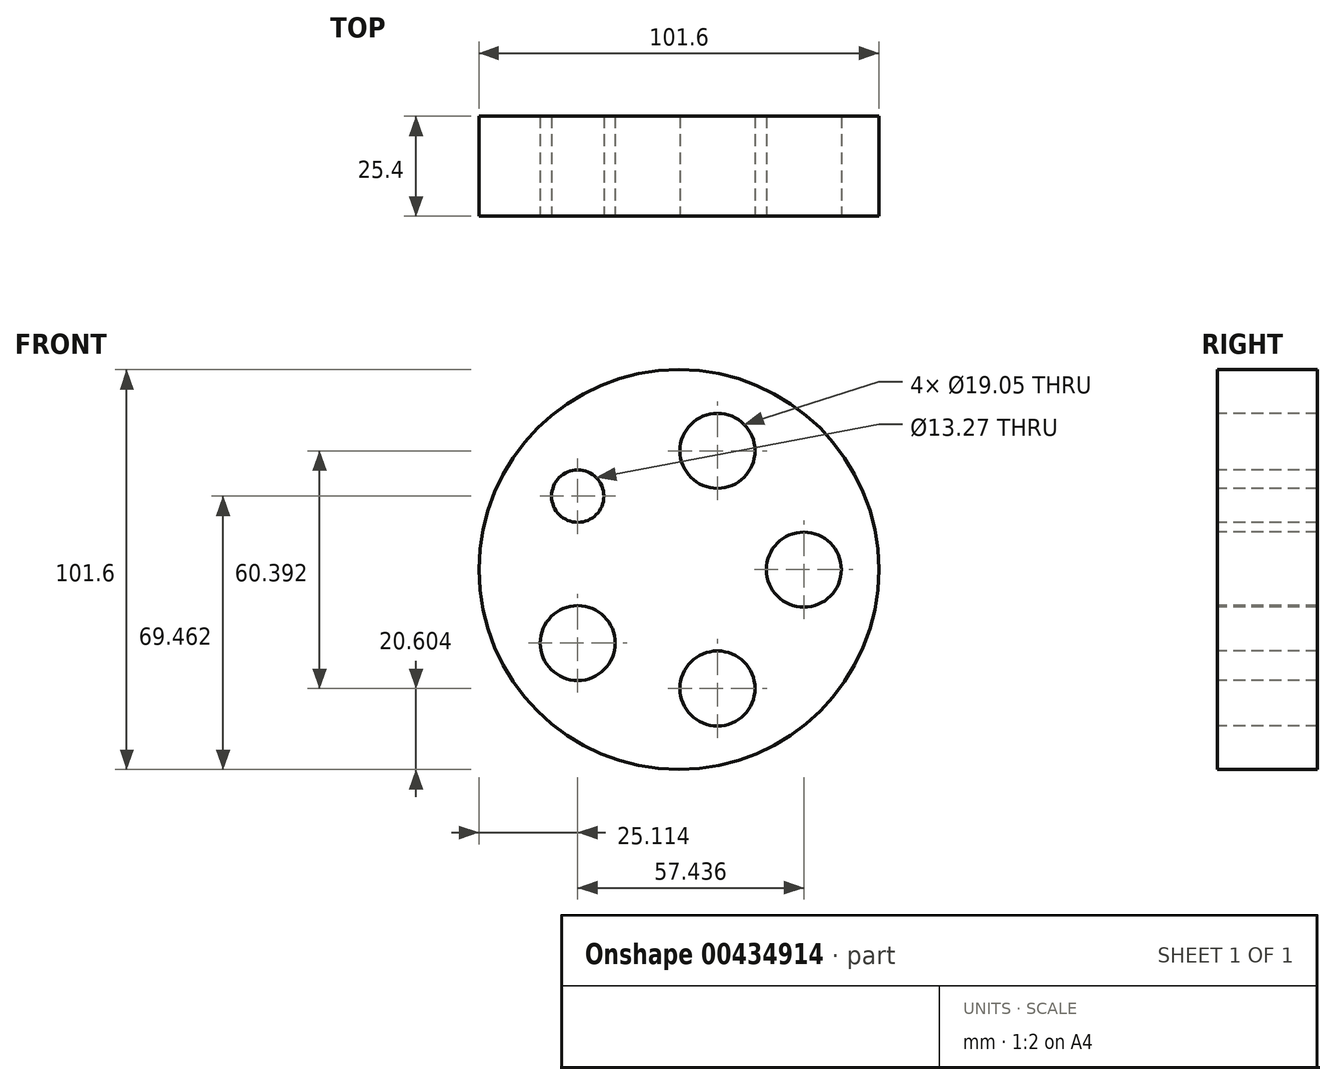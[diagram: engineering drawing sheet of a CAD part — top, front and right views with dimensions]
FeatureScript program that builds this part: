
annotation { "Feature Type Name" : "Feature", "Feature Type Description" : "" }
export const myFeature = defineFeature(function(context is Context, id is Id, definition is map)
    precondition{}
    {
        {
            var Q0;
            Q0=qCreatedBy(makeId("Front.planeOp"),FACE);
            var sketch = newSketch(context, id + "F0", { "sketchPlane" : qUnion([Q0])});
            skCircle(sketch, "E0", {"center": v(0, 0) * mm, "radius": 50.8 * mm});
            skCircle(sketch, "E1", {"center": v(0, 0) * mm, "radius": 31.75 * mm, "construction": true});
            skLineSegment(sketch, "E2.0", {"start": v(31.75, 0) * mm, "end": v(15.88, -27.5) * mm});
            skLineSegment(sketch, "E2.1", {"start": v(15.88, -27.5) * mm, "end": v(-15.87, -27.5) * mm});
            skLineSegment(sketch, "E2.2", {"start": v(-15.87, -27.5) * mm, "end": v(-31.75, 0) * mm});
            skLineSegment(sketch, "E2.3", {"start": v(-31.75, 0) * mm, "end": v(-15.88, 27.5) * mm});
            skLineSegment(sketch, "E2.4", {"start": v(-15.88, 27.5) * mm, "end": v(15.87, 27.5) * mm});
            skLineSegment(sketch, "E2.5", {"start": v(15.87, 27.5) * mm, "end": v(31.75, 0) * mm});
            skSolve(sketch);
        }
        {
            var Q0;
            Q0 = qSketchRegion(id + "F0", true);
            var Q1;
            Q1=makeQuery(id+"F0.imprint","IMPRINT",FACE,{"disambiguationData":[TD([[makeQuery(id+"F0.imprint","IMPRINT",EDGE,{"derivedFrom":sQuery(id+"F0.wireOp",EDGE,"E2.0")}),-1.0]])]});
            extrude(context, id + "F1", {"entities" : qUnion([Q0, Q1]), "depth" : 25.4 * mm});
        }
        {
            var Q0;
            Q0=makeQuery(id+"F1.opExtrude","CAP_FACE",FACE,{"disambiguationData":[OSD([sQuery(id+"F0.wireOp",EDGE,"E0")])],"isStart":false});
            var sketch = newSketch(context, id + "F2", { "sketchPlane" : qUnion([Q0])});
            skCircle(sketch, "E3", {"center": v(0, 0) * mm, "radius": 31.75 * mm, "construction": true});
            skLineSegment(sketch, "E4.0", {"start": v(31.75, 0) * mm, "end": v(9.81, -30.2) * mm});
            skLineSegment(sketch, "E4.1", {"start": v(9.81, -30.2) * mm, "end": v(-25.69, -18.66) * mm});
            skLineSegment(sketch, "E4.2", {"start": v(-25.69, -18.66) * mm, "end": v(-25.69, 18.66) * mm});
            skLineSegment(sketch, "E4.3", {"start": v(-25.69, 18.66) * mm, "end": v(9.81, 30.2) * mm});
            skLineSegment(sketch, "E4.4", {"start": v(9.81, 30.2) * mm, "end": v(31.75, 0) * mm});
            skCircle(sketch, "E5", {"center": v(9.81, 30.2) * mm, "radius": 3.18 * mm});
            skCircle(sketch, "E6", {"center": v(31.75, 0) * mm, "radius": 9.53 * mm});
            skCircle(sketch, "E7", {"center": v(9.81, -30.2) * mm, "radius": 9.53 * mm});
            skCircle(sketch, "E8", {"center": v(-25.69, 18.66) * mm, "radius": 9.53 * mm});
            skCircle(sketch, "E9", {"center": v(-25.69, -18.66) * mm, "radius": 8.93 * mm});
            skSolve(sketch);
        }
        {
            var Q0;
            Q0=sQuery(id+"F2.wireOp",VERTEX,"E5.center");
            var Q1;
            Q1=sQuery(id+"F2.wireOp",VERTEX,"E6.center");
            var Q2;
            Q2=sQuery(id+"F2.wireOp",VERTEX,"E9.center");
            var Q3;
            Q3=sQuery(id+"F2.wireOp",VERTEX,"E7.center");
            var Q4;
            Q4=makeQuery(id+"F1.opExtrude","SWEPT_BODY",BODY,{"disambiguationData":[OSD([sQuery(id+"F0.wireOp",EDGE,"E0")])]});
            hole(context, id + "F3", {"style" : HoleStyle.SIMPLE, "endStyle" : HoleEndStyle.THROUGH, "holeDiameter" : 19.05 * mm, "isTappedThrough" : true, "tappedDepth" : 12.7 * mm, "tapClearance" : 3, "locations" : qUnion([Q0, Q1, Q2, Q3]), "scope" : qUnion([Q4])});
        }
        {
            var Q0;
            Q0=makeQuery(id+"F1.opExtrude","CAP_FACE",FACE,{"disambiguationData":[OSD([sQuery(id+"F0.wireOp",EDGE,"E0")])],"isStart":false});
            var sketch = newSketch(context, id + "F4", { "sketchPlane" : qUnion([Q0])});
            skCircle(sketch, "E10.cCircle", {"center": v(0, 0) * mm, "radius": 31.75 * mm, "construction": true});
            skLineSegment(sketch, "E10.0", {"start": v(9.81, 30.2) * mm, "end": v(31.75, 0) * mm, "construction": true});
            skLineSegment(sketch, "E10.1", {"start": v(31.75, 0) * mm, "end": v(9.81, -30.2) * mm, "construction": true});
            skLineSegment(sketch, "E10.2", {"start": v(9.81, -30.2) * mm, "end": v(-25.69, -18.66) * mm, "construction": true});
            skLineSegment(sketch, "E10.3", {"start": v(-25.69, -18.66) * mm, "end": v(-25.69, 18.66) * mm, "construction": true});
            skLineSegment(sketch, "E10.4", {"start": v(-25.69, 18.66) * mm, "end": v(9.81, 30.2) * mm, "construction": true});
            skCircle(sketch, "E11", {"center": v(-25.69, 18.66) * mm, "radius": 6.64 * mm, "construction": true});
            skCircle(sketch, "E12", {"center": v(-25.69, 18.66) * mm, "radius": 6.63 * mm});
            skSolve(sketch);
        }
        {
            var Q0;
            Q0 = qSketchRegion(id + "F4", true);
            extrude(context, id + "F5", {"entities" : qUnion([Q0]), "operationType" : NewBodyOperationType.ADD, "depth" : 25.4 * mm});
        }
        {
            var Q0;
            Q0=makeQuery(id+"F1.opExtrude","CAP_FACE",FACE,{"disambiguationData":[OSD([sQuery(id+"F0.wireOp",EDGE,"E0")])],"isStart":false});
            var sketch = newSketch(context, id + "F6", { "sketchPlane" : qUnion([Q0])});
            skCircle(sketch, "E13", {"center": v(-25.69, 18.66) * mm, "radius": 3.17 * mm});
            skSolve(sketch);
        }
        {
            var Q0;
            Q0 = qSketchRegion(id + "F6", true);
            extrude(context, id + "F7", {"entities" : qUnion([Q0]), "operationType" : NewBodyOperationType.ADD, "depth" : 25.4 * mm});
        }
        {
            var Q0;
            Q0=makeQuery(id+"F5.opExtrude","CAP_FACE",FACE,{"disambiguationData":[OSD([sQuery(id+"F4.wireOp",EDGE,"E12")])],"isStart":false});
            extrude(context, id + "F8", {"entities" : qUnion([Q0]), "operationType" : NewBodyOperationType.REMOVE, "oppositeDirection" : true, "depth" : 101.6 * mm});
        }
    });
